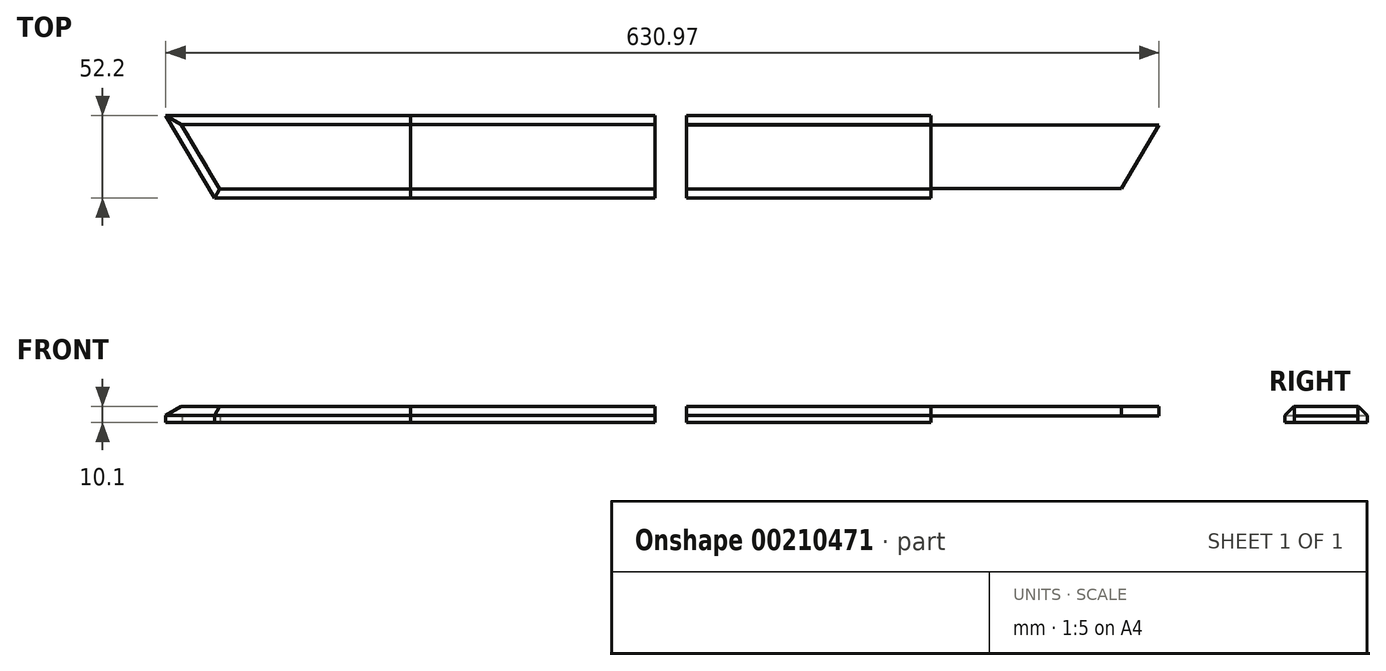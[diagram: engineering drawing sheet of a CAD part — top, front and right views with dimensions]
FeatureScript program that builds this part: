
annotation { "Feature Type Name" : "Feature", "Feature Type Description" : "" }
export const myFeature = defineFeature(function(context is Context, id is Id, definition is map)
    precondition{}
    {
        {
            var Q0;
            Q0=qCreatedBy(makeId("Top.planeOp"),FACE);
            var sketch = newSketch(context, id + "F0", { "sketchPlane" : qUnion([Q0])});
            skLineSegment(sketch, "E0", {"start": v(0, 0) * mm, "end": v(-10, 0) * mm});
            skLineSegment(sketch, "E1", {"start": v(-10, 0) * mm, "end": v(-10, 40.2) * mm});
            skLineSegment(sketch, "E2", {"start": v(-10, 40.2) * mm, "end": v(-310.2, 40.2) * mm});
            skLineSegment(sketch, "E3", {"start": v(-310.2, 40.2) * mm, "end": v(-286.2, 0) * mm});
            skLineSegment(sketch, "E4", {"start": v(-286.2, 0) * mm, "end": v(-10, 0) * mm});
            skLineSegment(sketch, "E5", {"start": v(-10, 40.2) * mm, "end": v(-10, 46.2) * mm});
            skLineSegment(sketch, "E6", {"start": v(-10, 46.2) * mm, "end": v(-320.77, 46.2) * mm});
            skLineSegment(sketch, "E7", {"start": v(-320.77, 46.2) * mm, "end": v(-289.6, -6) * mm});
            skLineSegment(sketch, "E8", {"start": v(-289.6, -6) * mm, "end": v(-10, -6) * mm});
            skLineSegment(sketch, "E9", {"start": v(-10, -6) * mm, "end": v(-10, 0) * mm});
            skLineSegment(sketch, "E10", {"start": v(0, 0) * mm, "end": v(0, 40) * mm});
            skLineSegment(sketch, "E11.MirrorCS", {"start": v(10, 0) * mm, "end": v(10, 40.2) * mm});
            skLineSegment(sketch, "E12.MirrorCS", {"start": v(10, 40.2) * mm, "end": v(10, 46.2) * mm});
            skLineSegment(sketch, "E13.MirrorCS", {"start": v(10, 40.2) * mm, "end": v(310.2, 40.2) * mm});
            skLineSegment(sketch, "E14.MirrorCS", {"start": v(10, 46.2) * mm, "end": v(320.77, 46.2) * mm});
            skLineSegment(sketch, "E15.MirrorCS", {"start": v(10, -6) * mm, "end": v(10, 0) * mm});
            skLineSegment(sketch, "E16.MirrorCS", {"start": v(289.6, -6) * mm, "end": v(10, -6) * mm});
            skLineSegment(sketch, "E17.MirrorCS", {"start": v(286.2, 0) * mm, "end": v(10, 0) * mm});
            skLineSegment(sketch, "E18.MirrorCS", {"start": v(310.2, 40.2) * mm, "end": v(286.2, 0) * mm});
            skLineSegment(sketch, "E19.MirrorCS", {"start": v(320.77, 46.2) * mm, "end": v(289.6, -6) * mm});
            skLineSegment(sketch, "E20", {"start": v(-10, 46.2) * mm, "end": v(-165.39, 46.2) * mm});
            skLineSegment(sketch, "E21", {"start": v(-165.39, 46.2) * mm, "end": v(-165.39, -6) * mm});
            skLineSegment(sketch, "E22", {"start": v(10, 46.2) * mm, "end": v(165.39, 46.2) * mm});
            skLineSegment(sketch, "E23", {"start": v(165.39, 46.2) * mm, "end": v(165.39, 0) * mm});
            skLineSegment(sketch, "E24", {"start": v(165.39, 0) * mm, "end": v(165.39, -6) * mm});
            skSolve(sketch);
        }
        {
            var Q0;
            Q0=makeQuery(id+"F0.imprint","IMPRINT",FACE,{"disambiguationData":[TD([[makeQuery(id+"F0.imprint","IMPRINT",EDGE,{"derivedFrom":sQuery(id+"F0.wireOp",EDGE,"E2")}),-1.0]])]});
            var Q1;
            Q1=makeQuery(id+"F0.imprint","IMPRINT",FACE,{"disambiguationData":[TD([[makeQuery(id+"F0.imprint","IMPRINT",EDGE,{"derivedFrom":sQuery(id+"F0.wireOp",EDGE,"E1")}),1.0]])]});
            var Q2;
            Q2=makeQuery(id+"F0.imprint","IMPRINT",FACE,{"disambiguationData":[TD([[makeQuery(id+"F0.imprint","IMPRINT",EDGE,{"derivedFrom":sQuery(id+"F0.wireOp",EDGE,"E11.MirrorCS")}),-1.0]])]});
            var Q3;
            Q3=makeQuery(id+"F0.imprint","IMPRINT",FACE,{"disambiguationData":[TD([[makeQuery(id+"F0.imprint","IMPRINT",EDGE,{"derivedFrom":sQuery(id+"F0.wireOp",EDGE,"E12.MirrorCS")}),-1.0]])]});
            var Q4;
            {var subQ0=sQuery(id+"F0.wireOp",EDGE,"E9");Q4=makeQuery(id+"F0.imprint","IMPRINT",FACE,{"disambiguationData":[TD([[makeQuery(id+"F0.imprint","IMPRINT",EDGE,{"derivedFrom":subQ0}),1.0]])]});}
            var Q5;
            {var subQ0=sQuery(id+"F0.wireOp",EDGE,"E15.MirrorCS");Q5=makeQuery(id+"F0.imprint","IMPRINT",FACE,{"disambiguationData":[TD([[makeQuery(id+"F0.imprint","IMPRINT",EDGE,{"derivedFrom":subQ0}),-1.0]])]});}
            extrude(context, id + "F1", {"entities" : qUnion([Q0, Q1, Q2, Q3, Q4, Q5]), "depth" : 10.1 * mm});
        }
        {
            var Q0;
            {var subQ0=sQuery(id+"F0.wireOp",EDGE,"E3");Q0=makeQuery(id+"F0.imprint","IMPRINT",FACE,{"disambiguationData":[TD([[makeQuery(id+"F0.imprint","IMPRINT",EDGE,{"derivedFrom":subQ0}),1.0]])]});}
            var Q1;
            {var subQ1=sQuery(id+"F0.wireOp",EDGE,"E3");Q1=makeQuery(id+"F0.imprint","IMPRINT",FACE,{"disambiguationData":[TD([[makeQuery(id+"F0.imprint","IMPRINT",EDGE,{"derivedFrom":subQ1}),-1.0]])]});}
            var Q2;
            {var subQ4=sQuery(id+"F0.wireOp",EDGE,"E14.MirrorCS");Q2=makeQuery(id+"F0.imprint","IMPRINT",FACE,{"disambiguationData":[TD([[makeQuery(id+"F0.imprint","IMPRINT",EDGE,{"derivedFrom":subQ4}),-1.0]])]});}
            var Q3;
            {var subQ0=sQuery(id+"F0.wireOp",EDGE,"E18.MirrorCS");Q3=makeQuery(id+"F0.imprint","IMPRINT",FACE,{"disambiguationData":[TD([[makeQuery(id+"F0.imprint","IMPRINT",EDGE,{"derivedFrom":subQ0}),-1.0]])]});}
            extrude(context, id + "F2", {"entities" : qUnion([Q0, Q1, Q2, Q3]), "depth" : 10.1 * mm});
        }
        {
            var Q0;
            Q0=makeQuery(id+"F0.imprint","IMPRINT",FACE,{"disambiguationData":[TD([[makeQuery(id+"F0.imprint","IMPRINT",EDGE,{"derivedFrom":sQuery(id+"F0.wireOp",EDGE,"E1")}),1.0]])]});
            var Q1;
            {var subQ0=sQuery(id+"F0.wireOp",EDGE,"E3");Q1=makeQuery(id+"F0.imprint","IMPRINT",FACE,{"disambiguationData":[TD([[makeQuery(id+"F0.imprint","IMPRINT",EDGE,{"derivedFrom":subQ0}),1.0]])]});}
            var Q2;
            {var subQ0=sQuery(id+"F0.wireOp",EDGE,"E18.MirrorCS");Q2=makeQuery(id+"F0.imprint","IMPRINT",FACE,{"disambiguationData":[TD([[makeQuery(id+"F0.imprint","IMPRINT",EDGE,{"derivedFrom":subQ0}),-1.0]])]});}
            var Q3;
            {var subQ0=sQuery(id+"F0.wireOp",EDGE,"E11.MirrorCS");Q3=makeQuery(id+"F0.imprint","IMPRINT",FACE,{"disambiguationData":[TD([[makeQuery(id+"F0.imprint","IMPRINT",EDGE,{"derivedFrom":subQ0}),-1.0]])]});}
            extrude(context, id + "F3", {"entities" : qUnion([Q0, Q1, Q2, Q3]), "operationType" : NewBodyOperationType.REMOVE, "depth" : 4.1 * mm});
        }
        {
            var Q0;
            Q0=makeQuery(id+"F0.imprint","IMPRINT",FACE,{"disambiguationData":[TD([[makeQuery(id+"F0.imprint","IMPRINT",EDGE,{"derivedFrom":sQuery(id+"F0.wireOp",EDGE,"E11.MirrorCS")}),-1.0]])]});
            var Q1;
            {var subQ0=sQuery(id+"F0.wireOp",EDGE,"E3");Q1=makeQuery(id+"F0.imprint","IMPRINT",FACE,{"disambiguationData":[TD([[makeQuery(id+"F0.imprint","IMPRINT",EDGE,{"derivedFrom":subQ0}),1.0]])]});}
            var Q2;
            {var subQ0=sQuery(id+"F0.wireOp",EDGE,"E18.MirrorCS");Q2=makeQuery(id+"F0.imprint","IMPRINT",FACE,{"disambiguationData":[TD([[makeQuery(id+"F0.imprint","IMPRINT",EDGE,{"derivedFrom":subQ0}),-1.0]])]});}
            extrude(context, id + "F4", {"entities" : qUnion([Q0, Q1, Q2]), "operationType" : NewBodyOperationType.REMOVE, "depth" : 4.1 * mm});
        }
        {
            var Q0;
            Q0=makeQuery(id+"F1.opExtrude","CAP_EDGE",EDGE,{"disambiguationData":[OSD([sQuery(id+"F0.wireOp",EDGE,"E6")])],"isStart":false});
            var Q1;
            Q1=makeQuery(id+"F1.opExtrude","CAP_EDGE",EDGE,{"disambiguationData":[OSD([sQuery(id+"F0.wireOp",EDGE,"E7")])],"isStart":false});
            var Q2;
            Q2=makeQuery(id+"F1.opExtrude","CAP_EDGE",EDGE,{"disambiguationData":[OSD([sQuery(id+"F0.wireOp",EDGE,"E8")])],"isStart":false});
            var Q3;
            Q3=makeQuery(id+"F1.opExtrude","CAP_EDGE",EDGE,{"disambiguationData":[OSD([sQuery(id+"F0.wireOp",EDGE,"E16.MirrorCS")])],"isStart":false});
            var Q4;
            Q4=makeQuery(id+"F1.opExtrude","CAP_EDGE",EDGE,{"disambiguationData":[OSD([sQuery(id+"F0.wireOp",EDGE,"E14.MirrorCS")])],"isStart":false});
            var Q5;
            Q5=makeQuery(id+"F1.opExtrude","CAP_EDGE",EDGE,{"disambiguationData":[OSD([sQuery(id+"F0.wireOp",EDGE,"E19.MirrorCS")])],"isStart":false});
            var Q6;
            Q6=makeQuery(id+"F2.opExtrude","CAP_EDGE",EDGE,{"disambiguationData":[OSD([sQuery(id+"F0.wireOp",EDGE,"E16.MirrorCS")])],"isStart":false});
            var Q7;
            Q7=makeQuery(id+"F2.opExtrude","CAP_EDGE",EDGE,{"disambiguationData":[OSD([sQuery(id+"F0.wireOp",EDGE,"E19.MirrorCS")])],"isStart":false});
            var Q8;
            Q8=makeQuery(id+"F2.opExtrude","CAP_EDGE",EDGE,{"disambiguationData":[OSD([sQuery(id+"F0.wireOp",EDGE,"E14.MirrorCS")])],"isStart":false});
            var Q9;
            Q9=makeQuery(id+"F2.opExtrude","CAP_EDGE",EDGE,{"disambiguationData":[OSD([sQuery(id+"F0.wireOp",EDGE,"E6")])],"isStart":false});
            var Q10;
            Q10=makeQuery(id+"F2.opExtrude","CAP_EDGE",EDGE,{"disambiguationData":[OSD([sQuery(id+"F0.wireOp",EDGE,"E7")])],"isStart":false});
            var Q11;
            Q11=makeQuery(id+"F2.opExtrude","CAP_EDGE",EDGE,{"disambiguationData":[OSD([sQuery(id+"F0.wireOp",EDGE,"E8")])],"isStart":false});
            var Q12;
            Q12=makeQuery(id+"F1.opExtrude","CAP_EDGE",EDGE,{"disambiguationData":[OSD([sQuery(id+"F0.wireOp",EDGE,"E20")])],"isStart":false});
            var Q13;
            Q13=makeQuery(id+"F1.opExtrude","CAP_EDGE",EDGE,{"disambiguationData":[OSD([sQuery(id+"F0.wireOp",EDGE,"E22")])],"isStart":false});
            chamfer(context, id + "F5", {"entities" : qUnion([Q0, Q1, Q2, Q3, Q4, Q5, Q6, Q7, Q8, Q9, Q10, Q11, Q12, Q13]), "width" : 5.6 * mm, "tangentPropagation" : true});
        }
        {
            var Q0;
            {var subQ0=sQuery(id+"F0.wireOp",EDGE,"E3");Q0=makeQuery(id+"F0.imprint","IMPRINT",FACE,{"disambiguationData":[TD([[makeQuery(id+"F0.imprint","IMPRINT",EDGE,{"derivedFrom":subQ0}),1.0]])]});}
            extrude(context, id + "F6", {"entities" : qUnion([Q0]), "operationType" : NewBodyOperationType.REMOVE, "depth" : 4.1 * mm});
        }
        {
            var Q0;
            {var subQ0=sQuery(id+"F0.wireOp",EDGE,"E18.MirrorCS");Q0=makeQuery(id+"F0.imprint","IMPRINT",FACE,{"disambiguationData":[TD([[makeQuery(id+"F0.imprint","IMPRINT",EDGE,{"derivedFrom":subQ0}),-1.0]])]});}
            extrude(context, id + "F7", {"entities" : qUnion([Q0]), "operationType" : NewBodyOperationType.REMOVE, "depth" : 4.1 * mm});
        }
    });
